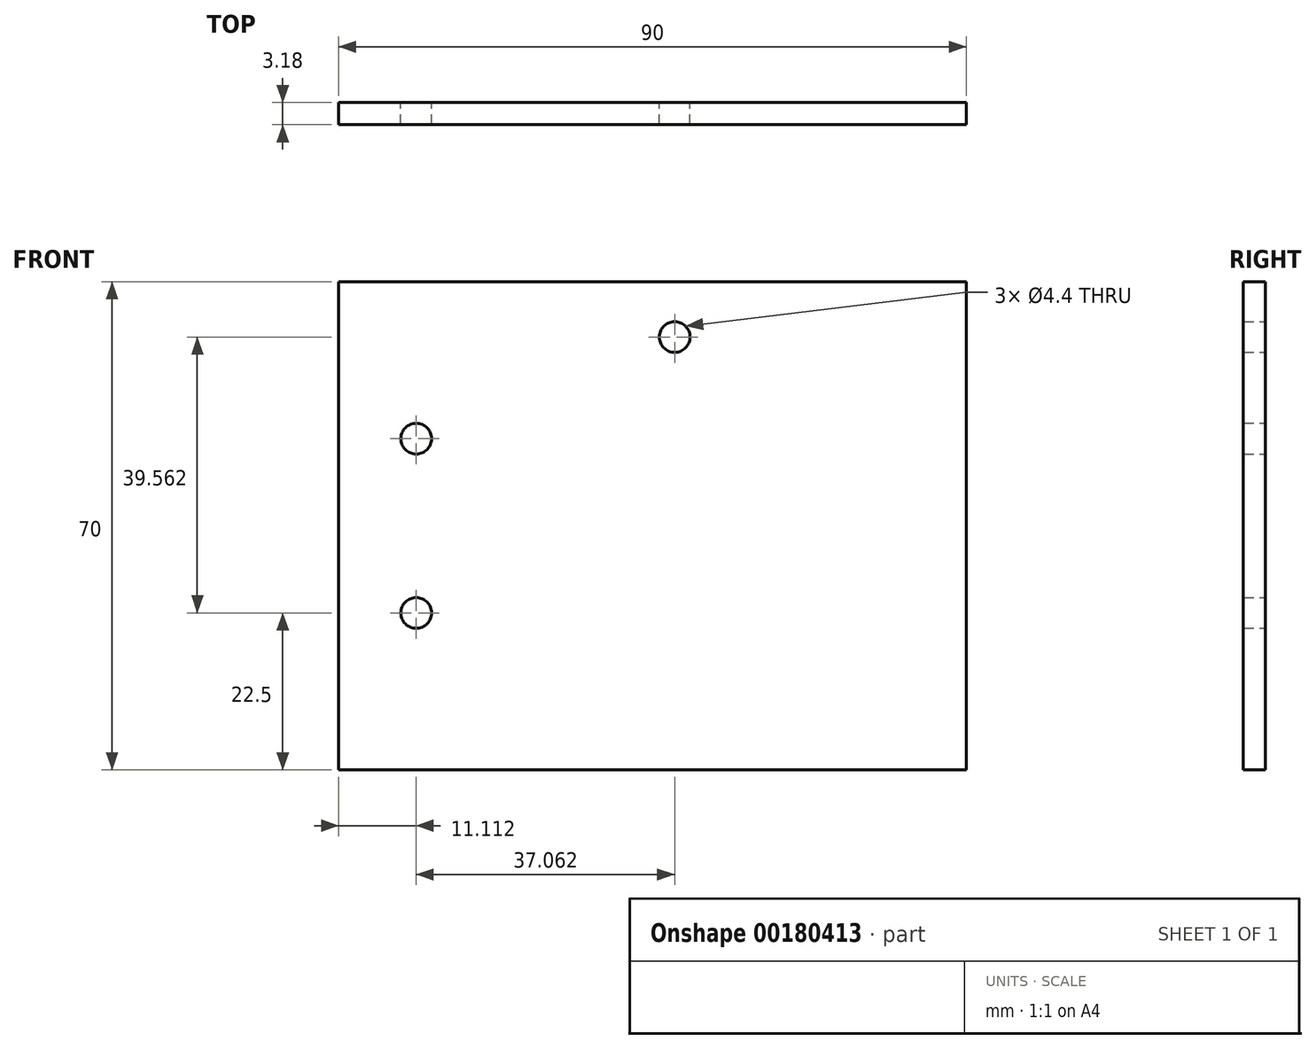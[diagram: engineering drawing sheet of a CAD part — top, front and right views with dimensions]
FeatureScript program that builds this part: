
annotation { "Feature Type Name" : "Feature", "Feature Type Description" : "" }
export const myFeature = defineFeature(function(context is Context, id is Id, definition is map)
    precondition{}
    {
        {
            var Q0;
            Q0=qCreatedBy(makeId("Top.planeOp"),FACE);
            var sketch = newSketch(context, id + "F0", { "sketchPlane" : qUnion([Q0])});
            skLineSegment(sketch, "E0.bottom", {"start": v(45, -1.59) * mm, "end": v(-45, -1.59) * mm});
            skLineSegment(sketch, "E0.top", {"start": v(45, 1.59) * mm, "end": v(-45, 1.59) * mm});
            skLineSegment(sketch, "E0.left", {"start": v(45, -1.59) * mm, "end": v(45, 1.59) * mm});
            skLineSegment(sketch, "E0.right", {"start": v(-45, -1.59) * mm, "end": v(-45, 1.59) * mm});
            skPoint(sketch, "E0.middle", {"position": v(0, 0) * mm});
            skSolve(sketch);
        }
        {
            var Q0;
            Q0 = qSketchRegion(id + "F0", true);
            extrude(context, id + "F1", {"entities" : qUnion([Q0]), "depth" : 70 * mm});
        }
        {
            var Q0;
            Q0=makeQuery(id+"F1.opExtrude","SWEPT_FACE",FACE,{"disambiguationData":[OSD([sQuery(id+"F0.wireOp",EDGE,"E0.top")])]});
            var sketch = newSketch(context, id + "F2", { "sketchPlane" : qUnion([Q0])});
            skPoint(sketch, "E1", {"position": v(33.89, 22.5) * mm});
            skPoint(sketch, "E2", {"position": v(33.89, 47.5) * mm});
            skPoint(sketch, "E3", {"position": v(-3.17, 62.06) * mm});
            skSolve(sketch);
        }
        {
            var Q0;
            Q0=sQuery(id+"F2.wireOp",VERTEX,"E1");
            var Q1;
            Q1=sQuery(id+"F2.wireOp",VERTEX,"E2");
            var Q2;
            Q2=sQuery(id+"F2.wireOp",VERTEX,"E3");
            var Q3;
            Q3=makeQuery(id+"F1.opExtrude","SWEPT_BODY",BODY,{"disambiguationData":[OSD([sQuery(id+"F0.wireOp",EDGE,"E0.bottom"),sQuery(id+"F0.wireOp",EDGE,"E0.top"),sQuery(id+"F0.wireOp",EDGE,"E0.left"),sQuery(id+"F0.wireOp",EDGE,"E0.right")])]});
            hole(context, id + "F3", {"style" : HoleStyle.SIMPLE, "endStyle" : HoleEndStyle.THROUGH, "standardTappedOrClearance" : lookupTablePath({ "standard" : "ISO", "fit" : "Normal", "size" : "M4", "type" : "Clearance" }), "standardBlindInLast" : lookupTablePath({ "fit" : "Standard", "standard" : "ISO", "size" : "M4", "type" : "Clearance" }), "holeDiameter" : 4.4 * mm, "locations" : qUnion([Q0, Q1, Q2]), "scope" : qUnion([Q3]), "isTappedThrough" : true});
        }
    });
